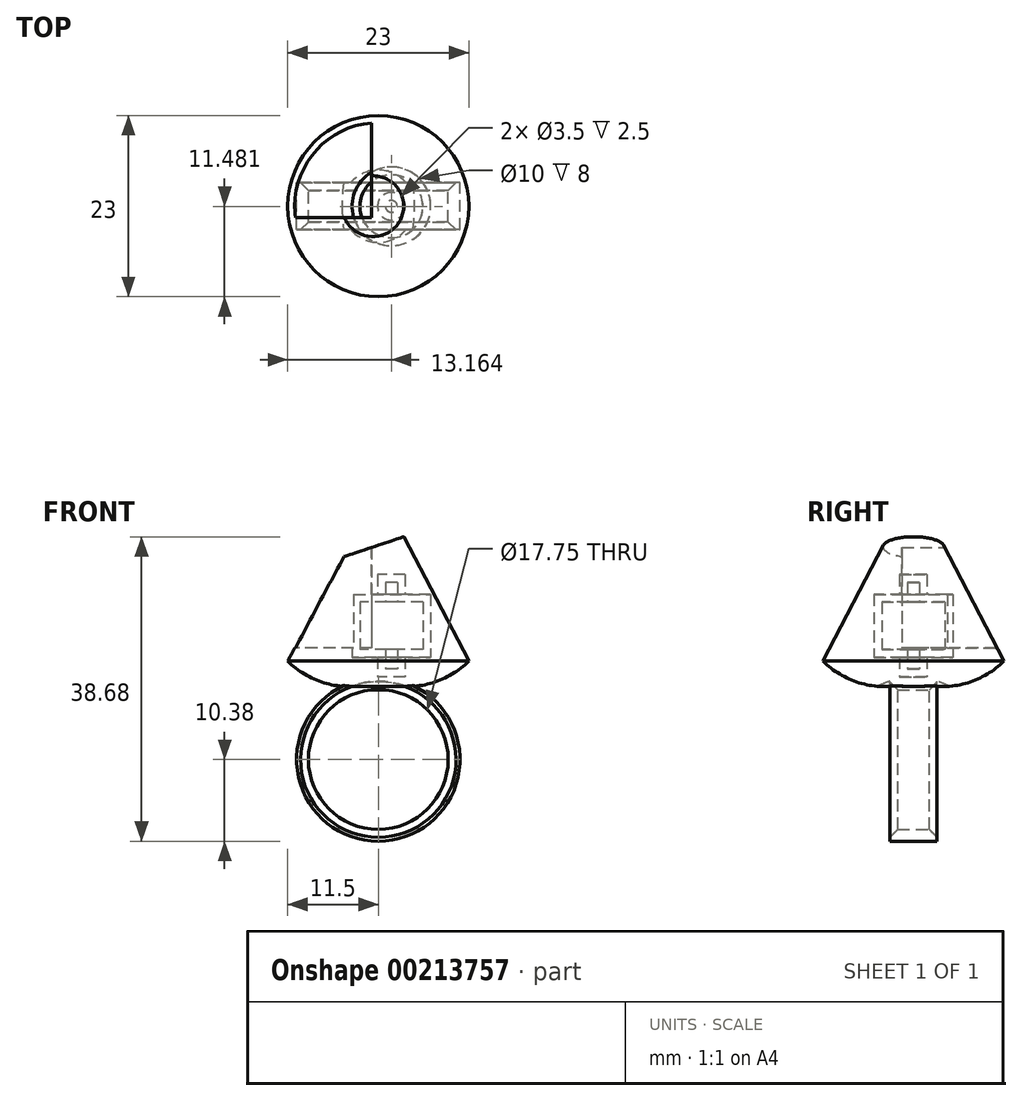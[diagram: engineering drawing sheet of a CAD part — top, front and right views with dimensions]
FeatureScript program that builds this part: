
annotation { "Feature Type Name" : "Feature", "Feature Type Description" : "" }
export const myFeature = defineFeature(function(context is Context, id is Id, definition is map)
    precondition{}
    {
        {
            var Q0;
            Q0=qCreatedBy(makeId("Front.planeOp"),FACE);
            var sketch = newSketch(context, id + "F0", { "sketchPlane" : qUnion([Q0])});
            skCircle(sketch, "E0", {"center": v(0, 0) * mm, "radius": 8.88 * mm});
            skCircle(sketch, "E1.0", {"center": v(0, 0) * mm, "radius": 10.38 * mm});
            skLineSegment(sketch, "E2", {"start": v(0, 9.3) * mm, "end": v(4.6, 9.3) * mm});
            skArc(sketch, "E3", {"start": v(4.6, 9.3) * mm, "mid": v(8.32, 10.3) * mm, "end": v(11.5, 12.5) * mm});
            skLineSegment(sketch, "E4", {"start": v(11.5, 12.5) * mm, "end": v(3.25, 28.3) * mm});
            skLineSegment(sketch, "E5", {"start": v(3.25, 28.3) * mm, "end": v(0, 28.3) * mm});
            skPoint(sketch, "E6", {"position": v(0, 9.3) * mm});
            skPoint(sketch, "E7.orphan", {"position": v(-4.6, 9.3) * mm});
            skLineSegment(sketch, "E8", {"start": v(0, 28.3) * mm, "end": v(0, 9.3) * mm});
            skSolve(sketch);
        }
        {
            var Q0;
            Q0=qCreatedBy(makeId("Top.planeOp"),FACE);
            var sketch = newSketch(context, id + "F1", { "sketchPlane" : qUnion([Q0])});
            skCircle(sketch, "E9", {"center": v(0, 0) * mm, "radius": 4.62 * mm});
            skSolve(sketch);
        }
        {
            var Q0;
            {var subQ1=sQuery(id+"F0.wireOp",EDGE,"E3");Q0=makeQuery(id+"F0.imprint","IMPRINT",FACE,{"disambiguationData":[TD([[makeQuery(id+"F0.imprint","IMPRINT",EDGE,{"derivedFrom":subQ1}),1.0]])]});}
            var Q1;
            Q1=sQuery(id+"F1.wireOp",EDGE,"E9");
            revolve(context, id + "F2", {"entities" : qUnion([Q0]), "axis" : qUnion([Q1]), "revolveType" : RevolveType.FULL});
        }
        {
            var Q0;
            Q0=makeQuery(id+"F0.imprint","IMPRINT",FACE,{"disambiguationData":[TD([[makeQuery(id+"F0.imprint","IMPRINT",EDGE,{"derivedFrom":sQuery(id+"F0.wireOp",EDGE,"E0")}),-1.0]])]});
            var Q1;
            {var subQ0=sQuery(id+"F0.wireOp",EDGE,"E2");Q1=makeQuery(id+"F0.imprint","IMPRINT",FACE,{"disambiguationData":[TD([[makeQuery(id+"F0.imprint","IMPRINT",EDGE,{"derivedFrom":subQ0}),1.0]])]});}
            extrude(context, id + "F3", {"entities" : qUnion([Q0, Q1]), "operationType" : NewBodyOperationType.ADD, "depth" : 3 * mm, "hasSecondDirection" : true, "secondDirectionOppositeDirection" : true, "secondDirectionDepth" : 3 * mm});
        }
        {
            var Q0;
            Q0=makeQuery(id+"F3.opExtrude","CAP_EDGE",EDGE,{"disambiguationData":[OSD([sQuery(id+"F0.wireOp",EDGE,"E0")])],"isStart":false});
            var Q1;
            Q1=makeQuery(id+"F3.opExtrude","CAP_EDGE",EDGE,{"disambiguationData":[OSD([sQuery(id+"F0.wireOp",EDGE,"E0")])],"isStart":true});
            chamfer(context, id + "F4", {"entities" : qUnion([Q0, Q1]), "width" : 1 * mm, "tangentPropagation" : true});
        }
        {
            var Q0;
            Q0=makeQuery(id+"F2.opRevolve","SWEPT_FACE",FACE,{"disambiguationData":[OSD([sQuery(id+"F0.wireOp",EDGE,"E5")])]});
            var sketch = newSketch(context, id + "F5", { "sketchPlane" : qUnion([Q0])});
            skLineSegment(sketch, "E10", {"start": v(-16.5, -1.45) * mm, "end": v(-0.89, 14.49) * mm});
            skLineSegment(sketch, "E11", {"start": v(-0.89, -1.45) * mm, "end": v(-0.89, 14.49) * mm});
            skPoint(sketch, "E12.start.orphan", {"position": v(0, 15.39) * mm});
            skPoint(sketch, "E13.orphan", {"position": v(0, -1.44) * mm});
            skLineSegment(sketch, "E14", {"start": v(-0.89, -1.45) * mm, "end": v(-16.5, -1.45) * mm});
            skSolve(sketch);
        }
        {
            var Q0;
            {var subQ0=sQuery(id+"F5.wireOp",EDGE,"E10");Q0=makeQuery(id+"F5.imprint","IMPRINT",FACE,{"disambiguationData":[TD([[makeQuery(id+"F5.imprint","IMPRINT",EDGE,{"derivedFrom":subQ0}),-1.0]])]});}
            var Q1;
            {var subQ0=sQuery(id+"F5.wireOp",EDGE,"E12");var subQ1=sQuery(id+"F5.wireOp",EDGE,"Eov0RMoM-jhBU-ptdb-pCwg-A5iMRD1cpr1U");var subQ2=makeQuery(id+"F5.imprint","INTERSECT",VERTEX,{"derivedFrom":[subQ1,subQ0]});Q1=makeQuery(id+"F5.imprint","IMPRINT",FACE,{"disambiguationData":[TD([[makeQuery(id+"F5.imprint","IMPRINT",EDGE,{"disambiguationData":[TD([[subQ2,-1.0]])],"derivedFrom":subQ1}),-1.0]])]});}
            var Q2;
            {var subQ0=sQuery(id+"F5.wireOp",EDGE,"E14");var subQ1=sQuery(id+"F5.wireOp",EDGE,"E11");var subQ2=makeQuery(id+"F5.imprint","INTERSECT",VERTEX,{"derivedFrom":[subQ1,subQ0]});Q2=makeQuery(id+"F5.imprint","IMPRINT",FACE,{"disambiguationData":[TD([[makeQuery(id+"F5.imprint","IMPRINT",EDGE,{"disambiguationData":[TD([[subQ2,-1.0]])],"derivedFrom":subQ1}),1.0]])]});}
            extrude(context, id + "F6", {"entities" : qUnion([Q0, Q1, Q2]), "operationType" : NewBodyOperationType.REMOVE, "oppositeDirection" : true, "depth" : 14.1 * mm});
        }
        {
            var Q0;
            Q0=qCreatedBy(makeId("Top.planeOp"),FACE);
            var sketch = newSketch(context, id + "F7", { "sketchPlane" : qUnion([Q0])});
            skCircle(sketch, "E15", {"center": v(1.66, -0.02) * mm, "radius": 4.5 * mm});
            skCircle(sketch, "E16", {"center": v(1.66, -0.02) * mm, "radius": 5 * mm});
            skCircle(sketch, "E17", {"center": v(1.66, -0.02) * mm, "radius": 0.75 * mm});
            skCircle(sketch, "E18.0", {"center": v(1.66, -0.02) * mm, "radius": 1.75 * mm});
            skCircle(sketch, "E19.0", {"center": v(1.66, -0.02) * mm, "radius": 4 * mm});
            skSolve(sketch);
        }
        {
            var Q0;
            Q0=makeQuery(id+"F7.imprint","IMPRINT",FACE,{"disambiguationData":[TD([[makeQuery(id+"F7.imprint","IMPRINT",EDGE,{"derivedFrom":sQuery(id+"F7.wireOp",EDGE,"E18.0")}),-1.0]])]});
            var Q1;
            Q1=makeQuery(id+"F7.imprint","IMPRINT",FACE,{"disambiguationData":[TD([[makeQuery(id+"F7.imprint","IMPRINT",EDGE,{"derivedFrom":sQuery(id+"F7.wireOp",EDGE,"E17")}),-1.0]])]});
            var Q2;
            Q2=makeQuery(id+"F7.imprint","IMPRINT",FACE,{"disambiguationData":[TD([[makeQuery(id+"F7.imprint","IMPRINT",EDGE,{"derivedFrom":sQuery(id+"F7.wireOp",EDGE,"E17")}),1.0]])]});
            extrude(context, id + "F8", {"entities" : qUnion([Q0, Q1, Q2]), "operationType" : NewBodyOperationType.ADD, "depth" : 20 * mm, "hasSecondDirection" : true, "secondDirectionOppositeDirection" : false, "secondDirectionDepth" : 13.5 * mm});
        }
        {
            var Q0;
            Q0=makeQuery(id+"F6.boolean.opBoolean","COPY",FACE,{"derivedFrom":makeQuery(id+"F6.opExtrude","SWEPT_FACE",FACE,{"disambiguationData":[OSD([sQuery(id+"F5.wireOp",EDGE,"E14")])]})});
            var sketch = newSketch(context, id + "F9", { "sketchPlane" : qUnion([Q0])});
            skLineSegment(sketch, "E20.bottom", {"start": v(2.3, 23.68) * mm, "end": v(4.1, 23.68) * mm});
            skLineSegment(sketch, "E20.top", {"start": v(2.3, 19.96) * mm, "end": v(4.1, 19.96) * mm});
            skLineSegment(sketch, "E20.left", {"start": v(2.3, 23.68) * mm, "end": v(2.3, 19.96) * mm});
            skLineSegment(sketch, "E20.right", {"start": v(4.1, 23.68) * mm, "end": v(4.1, 19.96) * mm});
            skLineSegment(sketch, "E21.bottom", {"start": v(4.51, 17.75) * mm, "end": v(6.14, 17.75) * mm});
            skLineSegment(sketch, "E21.top", {"start": v(4.51, 15.9) * mm, "end": v(6.14, 15.9) * mm});
            skLineSegment(sketch, "E21.left", {"start": v(4.51, 17.75) * mm, "end": v(4.51, 15.9) * mm});
            skLineSegment(sketch, "E21.right", {"start": v(6.14, 17.75) * mm, "end": v(6.14, 15.9) * mm});
            skSolve(sketch);
        }
        {
            var Q0;
            Q0=makeQuery(id+"F7.imprint","IMPRINT",FACE,{"disambiguationData":[TD([[makeQuery(id+"F7.imprint","IMPRINT",EDGE,{"derivedFrom":sQuery(id+"F7.wireOp",EDGE,"E15")}),-1.0]])]});
            var Q1;
            Q1=makeQuery(id+"F7.imprint","IMPRINT",FACE,{"disambiguationData":[TD([[makeQuery(id+"F7.imprint","IMPRINT",EDGE,{"derivedFrom":sQuery(id+"F7.wireOp",EDGE,"E15")}),1.0]])]});
            extrude(context, id + "F10", {"entities" : qUnion([Q0, Q1]), "operationType" : NewBodyOperationType.REMOVE, "depth" : 21 * mm, "hasSecondDirection" : true, "secondDirectionOppositeDirection" : false, "secondDirectionDepth" : 13 * mm});
        }
        {
            var Q0;
            Q0=makeQuery(id+"F7.imprint","IMPRINT",FACE,{"disambiguationData":[TD([[makeQuery(id+"F7.imprint","IMPRINT",EDGE,{"derivedFrom":sQuery(id+"F7.wireOp",EDGE,"E15")}),1.0]])]});
            var Q1;
            Q1=makeQuery(id+"F7.imprint","IMPRINT",FACE,{"disambiguationData":[TD([[makeQuery(id+"F7.imprint","IMPRINT",EDGE,{"derivedFrom":sQuery(id+"F7.wireOp",EDGE,"E17")}),-1.0]])]});
            var Q2;
            Q2=makeQuery(id+"F7.imprint","IMPRINT",FACE,{"disambiguationData":[TD([[makeQuery(id+"F7.imprint","IMPRINT",EDGE,{"derivedFrom":sQuery(id+"F7.wireOp",EDGE,"E17")}),1.0]])]});
            var Q3;
            Q3=makeQuery(id+"F7.imprint","IMPRINT",FACE,{"disambiguationData":[TD([[makeQuery(id+"F7.imprint","IMPRINT",EDGE,{"derivedFrom":sQuery(id+"F7.wireOp",EDGE,"E15")}),-1.0]])]});
            var Q4;
            Q4=makeQuery(id+"F7.imprint","IMPRINT",FACE,{"disambiguationData":[TD([[makeQuery(id+"F7.imprint","IMPRINT",EDGE,{"derivedFrom":sQuery(id+"F7.wireOp",EDGE,"E18.0")}),-1.0]])]});
            extrude(context, id + "F11", {"entities" : qUnion([Q0, Q1, Q2, Q3, Q4]), "operationType" : NewBodyOperationType.REMOVE, "depth" : 14 * mm, "hasSecondDirection" : true, "secondDirectionOppositeDirection" : false, "secondDirectionDepth" : 13 * mm});
        }
        {
            var Q0;
            Q0=makeQuery(id+"F7.imprint","IMPRINT",FACE,{"disambiguationData":[TD([[makeQuery(id+"F7.imprint","IMPRINT",EDGE,{"derivedFrom":sQuery(id+"F7.wireOp",EDGE,"E15")}),1.0]])]});
            var Q1;
            Q1=makeQuery(id+"F7.imprint","IMPRINT",FACE,{"disambiguationData":[TD([[makeQuery(id+"F7.imprint","IMPRINT",EDGE,{"derivedFrom":sQuery(id+"F7.wireOp",EDGE,"E17")}),-1.0]])]});
            var Q2;
            Q2=makeQuery(id+"F7.imprint","IMPRINT",FACE,{"disambiguationData":[TD([[makeQuery(id+"F7.imprint","IMPRINT",EDGE,{"derivedFrom":sQuery(id+"F7.wireOp",EDGE,"E17")}),1.0]])]});
            var Q3;
            Q3=makeQuery(id+"F7.imprint","IMPRINT",FACE,{"disambiguationData":[TD([[makeQuery(id+"F7.imprint","IMPRINT",EDGE,{"derivedFrom":sQuery(id+"F7.wireOp",EDGE,"E15")}),-1.0]])]});
            var Q4;
            Q4=makeQuery(id+"F7.imprint","IMPRINT",FACE,{"disambiguationData":[TD([[makeQuery(id+"F7.imprint","IMPRINT",EDGE,{"derivedFrom":sQuery(id+"F7.wireOp",EDGE,"E18.0")}),-1.0]])]});
            extrude(context, id + "F12", {"entities" : qUnion([Q0, Q1, Q2, Q3, Q4]), "operationType" : NewBodyOperationType.REMOVE, "depth" : 21 * mm, "hasSecondDirection" : true, "secondDirectionOppositeDirection" : false, "secondDirectionDepth" : 20 * mm});
        }
        {
            var Q0;
            Q0=makeQuery(id+"F7.imprint","IMPRINT",FACE,{"disambiguationData":[TD([[makeQuery(id+"F7.imprint","IMPRINT",EDGE,{"derivedFrom":sQuery(id+"F7.wireOp",EDGE,"E17")}),-1.0]])]});
            var Q1;
            Q1=makeQuery(id+"F7.imprint","IMPRINT",FACE,{"disambiguationData":[TD([[makeQuery(id+"F7.imprint","IMPRINT",EDGE,{"derivedFrom":sQuery(id+"F7.wireOp",EDGE,"E17")}),1.0]])]});
            extrude(context, id + "F13", {"entities" : qUnion([Q0, Q1]), "operationType" : NewBodyOperationType.REMOVE, "depth" : 13 * mm, "hasSecondDirection" : true, "secondDirectionOppositeDirection" : false, "secondDirectionDepth" : 10.5 * mm});
        }
        {
            var Q0;
            Q0=makeQuery(id+"F7.imprint","IMPRINT",FACE,{"disambiguationData":[TD([[makeQuery(id+"F7.imprint","IMPRINT",EDGE,{"derivedFrom":sQuery(id+"F7.wireOp",EDGE,"E17")}),1.0]])]});
            var Q1;
            Q1=makeQuery(id+"F7.imprint","IMPRINT",FACE,{"disambiguationData":[TD([[makeQuery(id+"F7.imprint","IMPRINT",EDGE,{"derivedFrom":sQuery(id+"F7.wireOp",EDGE,"E17")}),-1.0]])]});
            extrude(context, id + "F14", {"entities" : qUnion([Q0, Q1]), "operationType" : NewBodyOperationType.REMOVE, "depth" : 23.5 * mm, "hasSecondDirection" : true, "secondDirectionOppositeDirection" : false, "secondDirectionDepth" : 20 * mm});
        }
        {
            var Q0;
            Q0=makeQuery(id+"F7.imprint","IMPRINT",FACE,{"disambiguationData":[TD([[makeQuery(id+"F7.imprint","IMPRINT",EDGE,{"derivedFrom":sQuery(id+"F7.wireOp",EDGE,"E17")}),1.0]])]});
            extrude(context, id + "F15", {"entities" : qUnion([Q0]), "operationType" : NewBodyOperationType.ADD, "depth" : 14 * mm, "hasSecondDirection" : true, "secondDirectionOppositeDirection" : false, "secondDirectionDepth" : 11.5 * mm});
        }
        {
            var Q0;
            Q0=makeQuery(id+"F7.imprint","IMPRINT",FACE,{"disambiguationData":[TD([[makeQuery(id+"F7.imprint","IMPRINT",EDGE,{"derivedFrom":sQuery(id+"F7.wireOp",EDGE,"E17")}),1.0]])]});
            extrude(context, id + "F16", {"entities" : qUnion([Q0]), "operationType" : NewBodyOperationType.ADD, "depth" : 22.5 * mm, "hasSecondDirection" : true, "secondDirectionOppositeDirection" : false, "secondDirectionDepth" : 20 * mm});
        }
        {
            var Q0;
            Q0=makeQuery(id+"F6.boolean.opBoolean","COPY",FACE,{"derivedFrom":makeQuery(id+"F6.opExtrude","SWEPT_FACE",FACE,{"disambiguationData":[OSD([sQuery(id+"F5.wireOp",EDGE,"E14")])]})});
            var sketch = newSketch(context, id + "F17", { "sketchPlane" : qUnion([Q0])});
            skLineSegment(sketch, "E22.bottom", {"start": v(1.97, 26.87) * mm, "end": v(3.7, 26.87) * mm});
            skLineSegment(sketch, "E22.top", {"start": v(1.97, 22) * mm, "end": v(3.7, 22) * mm});
            skLineSegment(sketch, "E22.left", {"start": v(1.97, 26.87) * mm, "end": v(1.97, 22) * mm});
            skLineSegment(sketch, "E22.right", {"start": v(3.7, 26.87) * mm, "end": v(3.7, 22) * mm});
            skSolve(sketch);
        }
        {
            var Q0;
            Q0=makeQuery(id+"F6.boolean.opBoolean","COPY",FACE,{"derivedFrom":makeQuery(id+"F6.opExtrude","SWEPT_FACE",FACE,{"disambiguationData":[OSD([sQuery(id+"F5.wireOp",EDGE,"E11")])]})});
            var sketch = newSketch(context, id + "F18", { "sketchPlane" : qUnion([Q0])});
            skLineSegment(sketch, "E23", {"start": v(4.03, 29.48) * mm, "end": v(-7.11, 29.48) * mm});
            skLineSegment(sketch, "E24", {"start": v(-7.11, 29.48) * mm, "end": v(-9.2, 23.66) * mm});
            skLineSegment(sketch, "E25", {"start": v(-9.2, 23.66) * mm, "end": v(4.03, 29.48) * mm});
            skSolve(sketch);
        }
        {
            var Q0;
            Q0=qCreatedBy(makeId("Front.planeOp"),FACE);
            var sketch = newSketch(context, id + "F19", { "sketchPlane" : qUnion([Q0])});
            skLineSegment(sketch, "E26", {"start": v(-4.6, 25.7) * mm, "end": v(5, 28.9) * mm});
            skLineSegment(sketch, "E27", {"start": v(5, 28.9) * mm, "end": v(-4.39, 28.9) * mm});
            skLineSegment(sketch, "E28", {"start": v(-4.39, 28.9) * mm, "end": v(-4.6, 25.7) * mm});
            skSolve(sketch);
        }
        {
            var Q0;
            Q0=makeQuery(id+"F19.imprint","IMPRINT",FACE,{"disambiguationData":[TD([[makeQuery(id+"F19.imprint","IMPRINT",EDGE,{"derivedFrom":sQuery(id+"F19.wireOp",EDGE,"E26")}),1.0]])]});
            extrude(context, id + "F20", {"entities" : qUnion([Q0]), "operationType" : NewBodyOperationType.REMOVE, "oppositeDirection" : true, "depth" : 25 * mm, "hasSecondDirection" : true, "secondDirectionOppositeDirection" : false, "secondDirectionDepth" : 25 * mm});
        }
    });
